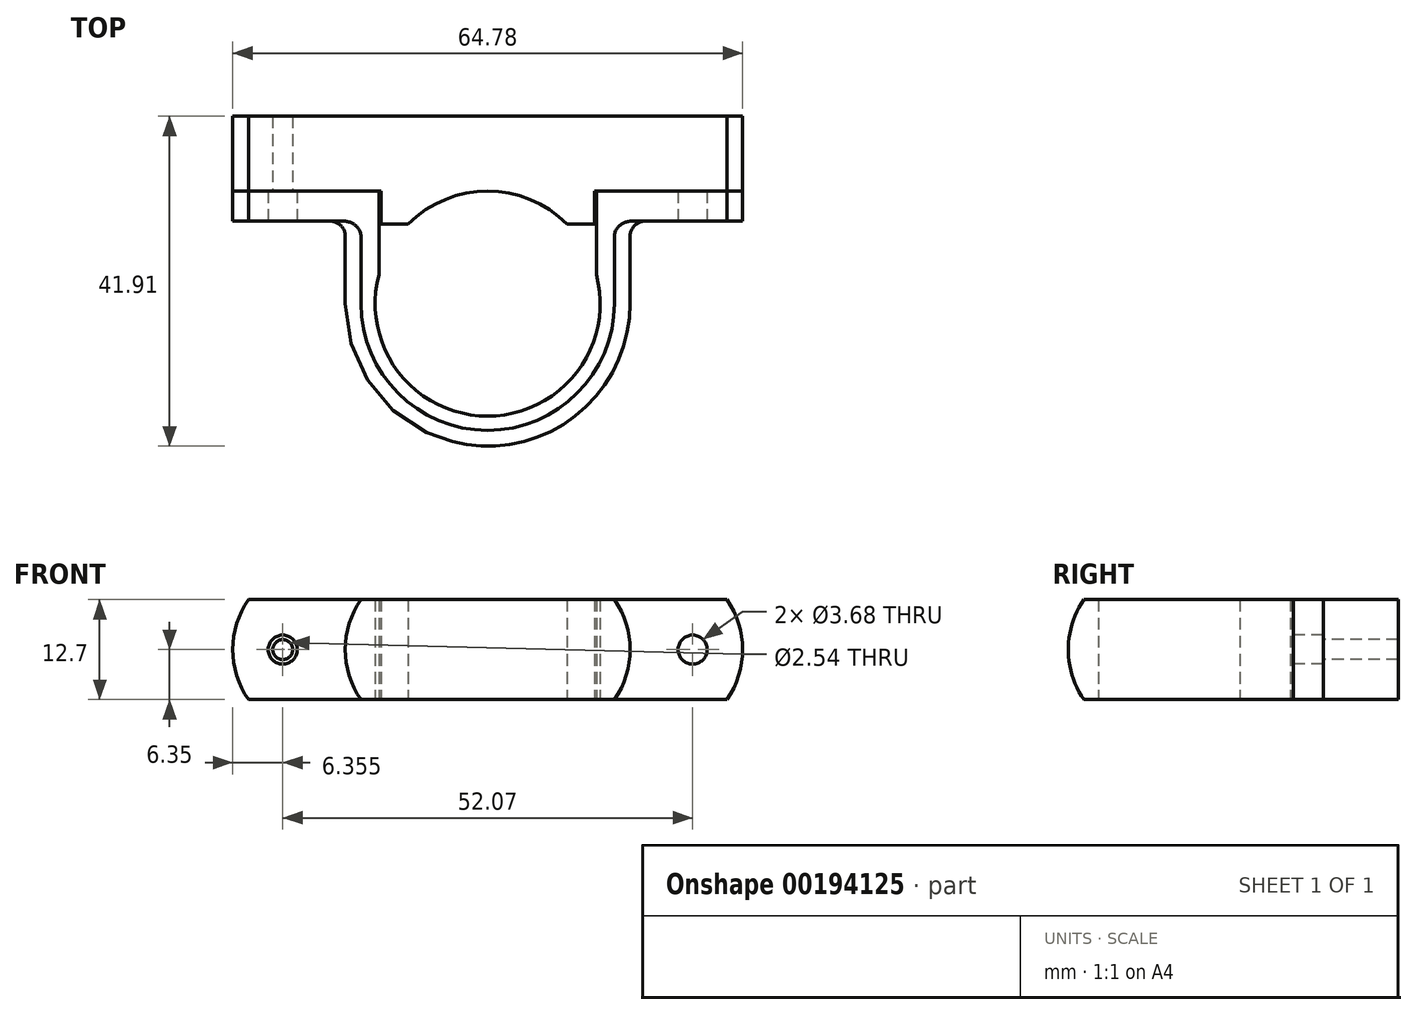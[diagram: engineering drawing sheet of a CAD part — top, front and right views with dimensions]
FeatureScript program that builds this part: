
annotation { "Feature Type Name" : "Feature", "Feature Type Description" : "" }
export const myFeature = defineFeature(function(context is Context, id is Id, definition is map)
    precondition{}
    {
        {
            var Q0;
            Q0=qCreatedBy(makeId("Top.planeOp"),FACE);
            var sketch = newSketch(context, id + "F0", { "sketchPlane" : qUnion([Q0])});
            skCircle(sketch, "E0", {"center": v(0, 0) * mm, "radius": 14.29 * mm, "construction": true});
            skLineSegment(sketch, "E1", {"start": v(-42.62, 14.29) * mm, "end": v(42.62, 14.29) * mm, "construction": true});
            skLineSegment(sketch, "E2", {"start": v(0, 0) * mm, "end": v(0, 14.29) * mm, "construction": true});
            skSolve(sketch);
        }
        {
            var Q0;
            Q0=qCreatedBy(makeId("Right.planeOp"),FACE);
            var sketch = newSketch(context, id + "F1", { "sketchPlane" : qUnion([Q0])});
            skLineSegment(sketch, "E3", {"start": v(16.1, 0) * mm, "end": v(14.29, 0) * mm});
            skLineSegment(sketch, "E4", {"start": v(14.29, 0) * mm, "end": v(14.29, 12.7) * mm});
            skLineSegment(sketch, "E5", {"start": v(14.29, 12.7) * mm, "end": v(16.1, 12.7) * mm});
            skArc(sketch, "E6", {"start": v(16.1, 0) * mm, "mid": v(18.1, 6.35) * mm, "end": v(16.1, 12.7) * mm});
            skLineSegment(sketch, "E7", {"start": v(16.1, 0) * mm, "end": v(20.54, 6.35) * mm, "construction": true});
            skLineSegment(sketch, "E8", {"start": v(0, 0) * mm, "end": v(0, 12.7) * mm, "construction": true});
            skLineSegment(sketch, "E9", {"start": v(18.1, 6.35) * mm, "end": v(14.29, 6.35) * mm, "construction": true});
            skSolve(sketch);
        }
        {
            var Q0;
            Q0=makeQuery(id+"F1.imprint","IMPRINT",FACE,{"disambiguationData":[TD([[makeQuery(id+"F1.imprint","IMPRINT",EDGE,{"derivedFrom":sQuery(id+"F1.wireOp",EDGE,"E3")}),-1.0]])]});
            var Q1;
            Q1=sQuery(id+"F1.wireOp",EDGE,"E8");
            revolve(context, id + "F2", {"entities" : qUnion([Q0]), "axis" : qUnion([Q1]), "revolveType" : RevolveType.FULL});
        }
        {
            var Q0;
            Q0=makeQuery(id+"F2.opRevolve","SWEPT_FACE",FACE,{"disambiguationData":[OSD([sQuery(id+"F1.wireOp",EDGE,"E5")])]});
            var sketch = newSketch(context, id + "F3", { "sketchPlane" : qUnion([Q0])});
            skArc(sketch, "E10", {"start": v(18.1, 0) * mm, "mid": v(0, 18.1) * mm, "end": v(-18.1, 0) * mm});
            skArc(sketch, "E11", {"start": v(14.29, 0) * mm, "mid": v(0, 14.29) * mm, "end": v(-14.29, 0) * mm});
            skLineSegment(sketch, "E12", {"start": v(14.29, 0) * mm, "end": v(18.1, 0) * mm});
            skLineSegment(sketch, "E13", {"start": v(-14.29, 0) * mm, "end": v(-18.1, 0) * mm});
            skLineSegment(sketch, "E14", {"start": v(-14.29, 0) * mm, "end": v(0, 0) * mm, "construction": true});
            skLineSegment(sketch, "E15", {"start": v(0, 0) * mm, "end": v(14.29, 0) * mm, "construction": true});
            skSolve(sketch);
        }
        {
            var Q0;
            {var subQ0=sQuery(id+"F3.wireOp",EDGE,"E10");Q0=makeQuery(id+"F3.imprint","IMPRINT",FACE,{"disambiguationData":[TD([[makeQuery(id+"F3.imprint","IMPRINT",EDGE,{"derivedFrom":subQ0}),1.0]])]});}
            var Q1;
            {var subQ0=sQuery(id+"F3.wireOp",EDGE,"E11");Q1=makeQuery(id+"F3.imprint","IMPRINT",FACE,{"disambiguationData":[TD([[makeQuery(id+"F3.imprint","IMPRINT",EDGE,{"derivedFrom":subQ0}),1.0]])]});}
            extrude(context, id + "F4", {"entities" : qUnion([Q0, Q1]), "operationType" : NewBodyOperationType.REMOVE, "endBound" : BoundingType.UP_TO_NEXT, "oppositeDirection" : true, "depth" : 25.4 * mm});
        }
        {
            var Q0;
            Q0=makeQuery(id+"F4.boolean.opBoolean","COPY",FACE,{"derivedFrom":makeQuery(id+"F4.opExtrude","SWEPT_FACE",FACE,{"disambiguationData":[OSD([sQuery(id+"F3.wireOp",EDGE,"E13")])]})});
            var Q1;
            Q1=makeQuery(id+"F4.boolean.opBoolean","COPY",FACE,{"derivedFrom":makeQuery(id+"F4.opExtrude","SWEPT_FACE",FACE,{"disambiguationData":[OSD([sQuery(id+"F3.wireOp",EDGE,"E12")])]})});
            var Q2;
            Q2=sQuery(id+"F0.wireOp",VERTEX,"E2.end");
            extrude(context, id + "F5", {"entities" : qUnion([Q0, Q1]), "operationType" : NewBodyOperationType.ADD, "endBound" : BoundingType.UP_TO_VERTEX, "endBoundEntityVertex" : qUnion([Q2]), "depth" : 25.4 * mm});
        }
        {
            var Q0;
            Q0=qCreatedBy(makeId("Top.planeOp"),FACE);
            var sketch = newSketch(context, id + "F6", { "sketchPlane" : qUnion([Q0])});
            skLineSegment(sketch, "E16", {"start": v(-13.8, 3.7) * mm, "end": v(0, 0) * mm, "construction": true});
            skLineSegment(sketch, "E17", {"start": v(0, 0) * mm, "end": v(13.8, 3.7) * mm, "construction": true});
            skLineSegment(sketch, "E18", {"start": v(0, 0) * mm, "end": v(-14.29, 0) * mm, "construction": true});
            skLineSegment(sketch, "E19", {"start": v(0, 0) * mm, "end": v(14.29, 0) * mm, "construction": true});
            skArc(sketch, "E20", {"start": v(-13.8, 3.7) * mm, "mid": v(-14.17, 1.86) * mm, "end": v(-14.29, 0) * mm});
            skArc(sketch, "E21", {"start": v(14.29, 0) * mm, "mid": v(14.17, 1.86) * mm, "end": v(13.8, 3.7) * mm});
            skLineSegment(sketch, "E22", {"start": v(-13.8, 3.7) * mm, "end": v(-13.8, 14.29) * mm});
            skLineSegment(sketch, "E23", {"start": v(-13.8, 14.29) * mm, "end": v(-14.29, 14.29) * mm});
            skLineSegment(sketch, "E24", {"start": v(-14.29, 14.29) * mm, "end": v(-14.29, 0) * mm});
            skLineSegment(sketch, "E25", {"start": v(13.8, 3.7) * mm, "end": v(13.8, 14.29) * mm});
            skLineSegment(sketch, "E26", {"start": v(13.8, 14.29) * mm, "end": v(14.29, 14.29) * mm});
            skLineSegment(sketch, "E27", {"start": v(14.29, 14.29) * mm, "end": v(14.29, 0) * mm});
            skLineSegment(sketch, "E28.bottom", {"start": v(-14.29, 14.29) * mm, "end": v(-32.39, 14.29) * mm});
            skLineSegment(sketch, "E28.top", {"start": v(-14.29, 10.48) * mm, "end": v(-32.39, 10.48) * mm});
            skLineSegment(sketch, "E28.left", {"start": v(-14.29, 14.29) * mm, "end": v(-14.29, 10.48) * mm});
            skLineSegment(sketch, "E28.right", {"start": v(-32.39, 14.29) * mm, "end": v(-32.39, 10.48) * mm});
            skLineSegment(sketch, "E29.bottom", {"start": v(14.29, 14.29) * mm, "end": v(32.39, 14.29) * mm});
            skLineSegment(sketch, "E29.top", {"start": v(14.29, 10.48) * mm, "end": v(32.39, 10.48) * mm});
            skLineSegment(sketch, "E29.left", {"start": v(14.29, 14.29) * mm, "end": v(14.29, 10.48) * mm});
            skLineSegment(sketch, "E29.right", {"start": v(32.39, 14.29) * mm, "end": v(32.39, 10.48) * mm});
            skLineSegment(sketch, "E30", {"start": v(-18.1, 0) * mm, "end": v(-14.29, 0) * mm, "construction": true});
            skSolve(sketch);
        }
        {
            var Q0;
            Q0 = qSketchRegion(id + "F6", true);
            var Q1;
            Q1=makeQuery(id+"F5.boolean.opBoolean","MERGE",FACE,{"derivedFrom":[makeQuery(id+"F2.opRevolve","SWEPT_FACE",FACE,{"disambiguationData":[OSD([sQuery(id+"F1.wireOp",EDGE,"E5")])]}),makeQuery(id+"F5.opExtrude","SWEPT_FACE",FACE,{"disambiguationData":[OSD([sQuery(id+"F3.wireOp",EDGE,"E12")])]}),makeQuery(id+"F5.opExtrude","SWEPT_FACE",FACE,{"disambiguationData":[OSD([sQuery(id+"F3.wireOp",EDGE,"E13")])]})]});
            extrude(context, id + "F7", {"entities" : qUnion([Q0]), "operationType" : NewBodyOperationType.ADD, "endBound" : BoundingType.UP_TO_SURFACE, "endBoundEntityFace" : qUnion([Q1]), "depth" : 25.4 * mm});
        }
        {
            var Q0;
            Q0=makeQuery(id+"F7.opExtrude","SWEPT_FACE",FACE,{"disambiguationData":[OSD([sQuery(id+"F6.wireOp",EDGE,"E28.top")])]});
            var sketch = newSketch(context, id + "F8", { "sketchPlane" : qUnion([Q0])});
            skArc(sketch, "E31", {"start": v(-30.38, 12.7) * mm, "mid": v(-32.39, 6.35) * mm, "end": v(-30.38, 0) * mm});
            skArc(sketch, "E32", {"start": v(30.38, 0) * mm, "mid": v(32.39, 6.35) * mm, "end": v(30.38, 12.7) * mm});
            skLineSegment(sketch, "E33", {"start": v(-30.38, 12.7) * mm, "end": v(-32.39, 12.7) * mm});
            skLineSegment(sketch, "E34", {"start": v(-32.39, 12.7) * mm, "end": v(-32.39, 0) * mm});
            skLineSegment(sketch, "E35", {"start": v(-32.39, 0) * mm, "end": v(-30.38, 0) * mm});
            skLineSegment(sketch, "E36", {"start": v(30.38, 12.7) * mm, "end": v(32.39, 12.7) * mm});
            skLineSegment(sketch, "E37", {"start": v(32.39, 12.7) * mm, "end": v(32.39, 0) * mm});
            skLineSegment(sketch, "E38", {"start": v(32.39, 0) * mm, "end": v(30.38, 0) * mm});
            skCircle(sketch, "E39", {"center": v(-26.04, 6.35) * mm, "radius": 6.35 * mm, "construction": true});
            skCircle(sketch, "E40", {"center": v(26.04, 6.35) * mm, "radius": 6.35 * mm, "construction": true});
            skCircle(sketch, "E41", {"center": v(-26.04, 6.35) * mm, "radius": 1.84 * mm});
            skCircle(sketch, "E42", {"center": v(26.04, 6.35) * mm, "radius": 1.84 * mm});
            skSolve(sketch);
        }
        {
            var Q0;
            Q0=makeQuery(id+"F8.imprint","IMPRINT",FACE,{"disambiguationData":[TD([[makeQuery(id+"F8.imprint","IMPRINT",EDGE,{"derivedFrom":sQuery(id+"F8.wireOp",EDGE,"E41")}),1.0]])]});
            var Q1;
            {var subQ0=sQuery(id+"F8.wireOp",EDGE,"E33");Q1=makeQuery(id+"F8.imprint","IMPRINT",FACE,{"disambiguationData":[TD([[makeQuery(id+"F8.imprint","IMPRINT",EDGE,{"derivedFrom":subQ0}),-1.0]])]});}
            var Q2;
            {var subQ0=sQuery(id+"F8.wireOp",EDGE,"E35");Q2=makeQuery(id+"F8.imprint","IMPRINT",FACE,{"disambiguationData":[TD([[makeQuery(id+"F8.imprint","IMPRINT",EDGE,{"derivedFrom":subQ0}),-1.0]])]});}
            var Q3;
            Q3=makeQuery(id+"F8.imprint","IMPRINT",FACE,{"disambiguationData":[TD([[makeQuery(id+"F8.imprint","IMPRINT",EDGE,{"derivedFrom":sQuery(id+"F8.wireOp",EDGE,"E42")}),1.0]])]});
            var Q4;
            {var subQ0=sQuery(id+"F8.wireOp",EDGE,"E36");Q4=makeQuery(id+"F8.imprint","IMPRINT",FACE,{"disambiguationData":[TD([[makeQuery(id+"F8.imprint","IMPRINT",EDGE,{"derivedFrom":subQ0}),-1.0]])]});}
            var Q5;
            {var subQ0=sQuery(id+"F8.wireOp",EDGE,"E38");Q5=makeQuery(id+"F8.imprint","IMPRINT",FACE,{"disambiguationData":[TD([[makeQuery(id+"F8.imprint","IMPRINT",EDGE,{"derivedFrom":subQ0}),-1.0]])]});}
            extrude(context, id + "F9", {"entities" : qUnion([Q0, Q1, Q2, Q3, Q4, Q5]), "operationType" : NewBodyOperationType.REMOVE, "endBound" : BoundingType.UP_TO_NEXT, "oppositeDirection" : true, "depth" : 25.4 * mm});
        }
        {
            var Q0;
            Q0=makeQuery(id+"F7.boolean.opBoolean","INTERSECT",EDGE,{"derivedFrom":[makeQuery(id+"F5.opExtrude","SWEPT_FACE",FACE,{"disambiguationData":[OSD([sQuery(id+"F1.wireOp",EDGE,"E6"),sQuery(id+"F3.wireOp",EDGE,"E13")])]}),makeQuery(id+"F7.opExtrude","SWEPT_FACE",FACE,{"disambiguationData":[OSD([sQuery(id+"F6.wireOp",EDGE,"E28.top")])]})]});
            var Q1;
            Q1=makeQuery(id+"F7.boolean.opBoolean","INTERSECT",EDGE,{"derivedFrom":[makeQuery(id+"F5.opExtrude","SWEPT_FACE",FACE,{"disambiguationData":[OSD([sQuery(id+"F1.wireOp",EDGE,"E6"),sQuery(id+"F3.wireOp",EDGE,"E12")])]}),makeQuery(id+"F7.opExtrude","SWEPT_FACE",FACE,{"disambiguationData":[OSD([sQuery(id+"F6.wireOp",EDGE,"E29.top")])]})]});
            fillet(context, id + "F10", {"entities" : qUnion([Q0, Q1]), "radius" : 1.9 * mm, "tangentPropagation" : true, "allowEdgeOverflow" : false});
        }
        {
            var Q0;
            Q0=qCreatedBy(makeId("Top.planeOp"),FACE);
            var sketch = newSketch(context, id + "F11", { "sketchPlane" : qUnion([Q0])});
            skLineSegment(sketch, "E43.bottom", {"start": v(-32.39, 23.81) * mm, "end": v(32.39, 23.81) * mm});
            skLineSegment(sketch, "E43.top", {"start": v(-32.39, 14.29) * mm, "end": v(32.39, 14.29) * mm});
            skLineSegment(sketch, "E43.left", {"start": v(-32.39, 23.81) * mm, "end": v(-32.39, 14.29) * mm});
            skLineSegment(sketch, "E43.right", {"start": v(32.39, 23.81) * mm, "end": v(32.39, 14.29) * mm});
            skArc(sketch, "E44", {"start": v(10.1, 10.1) * mm, "mid": v(0, 14.29) * mm, "end": v(-10.1, 10.1) * mm});
            skLineSegment(sketch, "E45", {"start": v(10.1, 10.1) * mm, "end": v(13.55, 10.1) * mm});
            skLineSegment(sketch, "E46", {"start": v(13.55, 10.1) * mm, "end": v(13.55, 14.29) * mm});
            skLineSegment(sketch, "E47", {"start": v(-10.1, 10.1) * mm, "end": v(-13.55, 10.1) * mm});
            skLineSegment(sketch, "E48", {"start": v(-13.55, 10.1) * mm, "end": v(-13.55, 14.29) * mm});
            skLineSegment(sketch, "E49", {"start": v(-10.1, 10.1) * mm, "end": v(0, 0) * mm, "construction": true});
            skLineSegment(sketch, "E50", {"start": v(0, 0) * mm, "end": v(10.1, 10.1) * mm, "construction": true});
            skLineSegment(sketch, "E51", {"start": v(-13.55, 10.1) * mm, "end": v(-13.8, 10.1) * mm, "construction": true});
            skLineSegment(sketch, "E52", {"start": v(13.55, 10.1) * mm, "end": v(13.8, 10.1) * mm, "construction": true});
            skSolve(sketch);
        }
        {
            var Q0;
            Q0 = qSketchRegion(id + "F11", true);
            var Q1;
            {var subQ0=sQuery(id+"F3.wireOp",EDGE,"E13");var subQ1=sQuery(id+"F3.wireOp",EDGE,"E12");var subQ2=sQuery(id+"F1.wireOp",EDGE,"E5");Q1=makeQuery(id+"F7.boolean.opBoolean","MERGE",FACE,{"derivedFrom":[makeQuery(id+"F5.boolean.opBoolean","MERGE",FACE,{"derivedFrom":[makeQuery(id+"F2.opRevolve","SWEPT_FACE",FACE,{"disambiguationData":[OSD([subQ2])]}),makeQuery(id+"F5.opExtrude","SWEPT_FACE",FACE,{"disambiguationData":[OSD([subQ1])]}),makeQuery(id+"F5.opExtrude","SWEPT_FACE",FACE,{"disambiguationData":[OSD([subQ0])]})]}),makeQuery(id+"F7.opExtrude","CAP_FACE",FACE,{"disambiguationData":[OSD([subQ2,subQ1,subQ0]),ownerDisambiguation([makeQuery(id+"F7.opExtrude","SWEPT_BODY",BODY,{"disambiguationData":[OSD([sQuery(id+"F6.wireOp",EDGE,"E20"),sQuery(id+"F6.wireOp",EDGE,"E22"),sQuery(id+"F6.wireOp",EDGE,"E23"),sQuery(id+"F6.wireOp",EDGE,"E24"),sQuery(id+"F6.wireOp",EDGE,"E28.bottom"),sQuery(id+"F6.wireOp",EDGE,"E28.top"),sQuery(id+"F6.wireOp",EDGE,"E28.right")])]})])],"isStart":false}),makeQuery(id+"F7.opExtrude","CAP_FACE",FACE,{"disambiguationData":[OSD([subQ2,subQ1,subQ0]),ownerDisambiguation([makeQuery(id+"F7.opExtrude","SWEPT_BODY",BODY,{"disambiguationData":[OSD([sQuery(id+"F6.wireOp",EDGE,"E21"),sQuery(id+"F6.wireOp",EDGE,"E25"),sQuery(id+"F6.wireOp",EDGE,"E26"),sQuery(id+"F6.wireOp",EDGE,"E27"),sQuery(id+"F6.wireOp",EDGE,"E29.bottom"),sQuery(id+"F6.wireOp",EDGE,"E29.top"),sQuery(id+"F6.wireOp",EDGE,"E29.right")])]})])],"isStart":false})]});}
            extrude(context, id + "F12", {"entities" : qUnion([Q0]), "endBound" : BoundingType.UP_TO_SURFACE, "endBoundEntityFace" : qUnion([Q1]), "depth" : 25.4 * mm});
        }
        {
            var Q0;
            {var subQ0=sQuery(id+"F11.wireOp",EDGE,"E43.top");Q0=makeQuery(id+"F12.opExtrude","SWEPT_FACE",FACE,{"disambiguationData":[OSD([subQ0]),TDD([makeQuery(id+"F11.imprint","IMPRINT",EDGE,{"disambiguationData":[TD([[makeQuery(id+"F11.imprint","INTERSECT",VERTEX,{"derivedFrom":[subQ0,sQuery(id+"F11.wireOp",EDGE,"E43.left")]}),-1.0]])],"derivedFrom":subQ0})])]});}
            var sketch = newSketch(context, id + "F13", { "sketchPlane" : qUnion([Q0])});
            skArc(sketch, "E53", {"start": v(-30.38, 12.7) * mm, "mid": v(-32.39, 6.35) * mm, "end": v(-30.38, 0) * mm});
            skLineSegment(sketch, "E54", {"start": v(-30.38, 0) * mm, "end": v(-32.39, 0) * mm});
            skLineSegment(sketch, "E55", {"start": v(-32.39, 0) * mm, "end": v(-32.39, 12.7) * mm});
            skLineSegment(sketch, "E56", {"start": v(-32.39, 12.7) * mm, "end": v(-30.38, 12.7) * mm});
            skCircle(sketch, "E57", {"center": v(-26.04, 6.35) * mm, "radius": 1.27 * mm});
            skArc(sketch, "E58.MirrorCS", {"start": v(30.38, 12.7) * mm, "mid": v(32.39, 6.35) * mm, "end": v(30.38, 0) * mm});
            skLineSegment(sketch, "E59.MirrorCS", {"start": v(30.38, 0) * mm, "end": v(32.39, 0) * mm});
            skLineSegment(sketch, "E60.MirrorCS", {"start": v(32.39, 12.7) * mm, "end": v(30.38, 12.7) * mm});
            skLineSegment(sketch, "E61.MirrorCS", {"start": v(32.39, 0) * mm, "end": v(32.39, 12.7) * mm});
            skCircle(sketch, "E62.MirrorC", {"center": v(26.04, 6.35) * mm, "radius": 1.27 * mm});
            skSolve(sketch);
        }
        {
            var Q0;
            {var subQ0=sQuery(id+"F13.wireOp",EDGE,"E56");Q0=makeQuery(id+"F13.imprint","IMPRINT",FACE,{"disambiguationData":[TD([[makeQuery(id+"F13.imprint","IMPRINT",EDGE,{"derivedFrom":subQ0}),1.0]])]});}
            var Q1;
            {var subQ0=sQuery(id+"F13.wireOp",EDGE,"E54");Q1=makeQuery(id+"F13.imprint","IMPRINT",FACE,{"disambiguationData":[TD([[makeQuery(id+"F13.imprint","IMPRINT",EDGE,{"derivedFrom":subQ0}),1.0]])]});}
            var Q2;
            Q2=makeQuery(id+"F13.imprint","IMPRINT",FACE,{"disambiguationData":[TD([[makeQuery(id+"F13.imprint","IMPRINT",EDGE,{"derivedFrom":sQuery(id+"F13.wireOp",EDGE,"E57")}),1.0]])]});
            var Q3;
            Q3=makeQuery(id+"F13.imprint","IMPRINT",FACE,{"disambiguationData":[TD([[makeQuery(id+"F13.imprint","IMPRINT",EDGE,{"derivedFrom":sQuery(id+"F13.wireOp",EDGE,"E62.MirrorC")}),-1.0]])]});
            var Q4;
            {var subQ0=sQuery(id+"F13.wireOp",EDGE,"E60.MirrorCS");Q4=makeQuery(id+"F13.imprint","IMPRINT",FACE,{"disambiguationData":[TD([[makeQuery(id+"F13.imprint","IMPRINT",EDGE,{"derivedFrom":subQ0}),1.0]])]});}
            var Q5;
            {var subQ0=sQuery(id+"F13.wireOp",EDGE,"E59.MirrorCS");Q5=makeQuery(id+"F13.imprint","IMPRINT",FACE,{"disambiguationData":[TD([[makeQuery(id+"F13.imprint","IMPRINT",EDGE,{"derivedFrom":subQ0}),1.0]])]});}
            extrude(context, id + "F14", {"entities" : qUnion([Q0, Q1, Q2, Q3, Q4, Q5]), "operationType" : NewBodyOperationType.REMOVE, "endBound" : BoundingType.UP_TO_NEXT, "oppositeDirection" : true, "depth" : 25.4 * mm});
        }
    });
